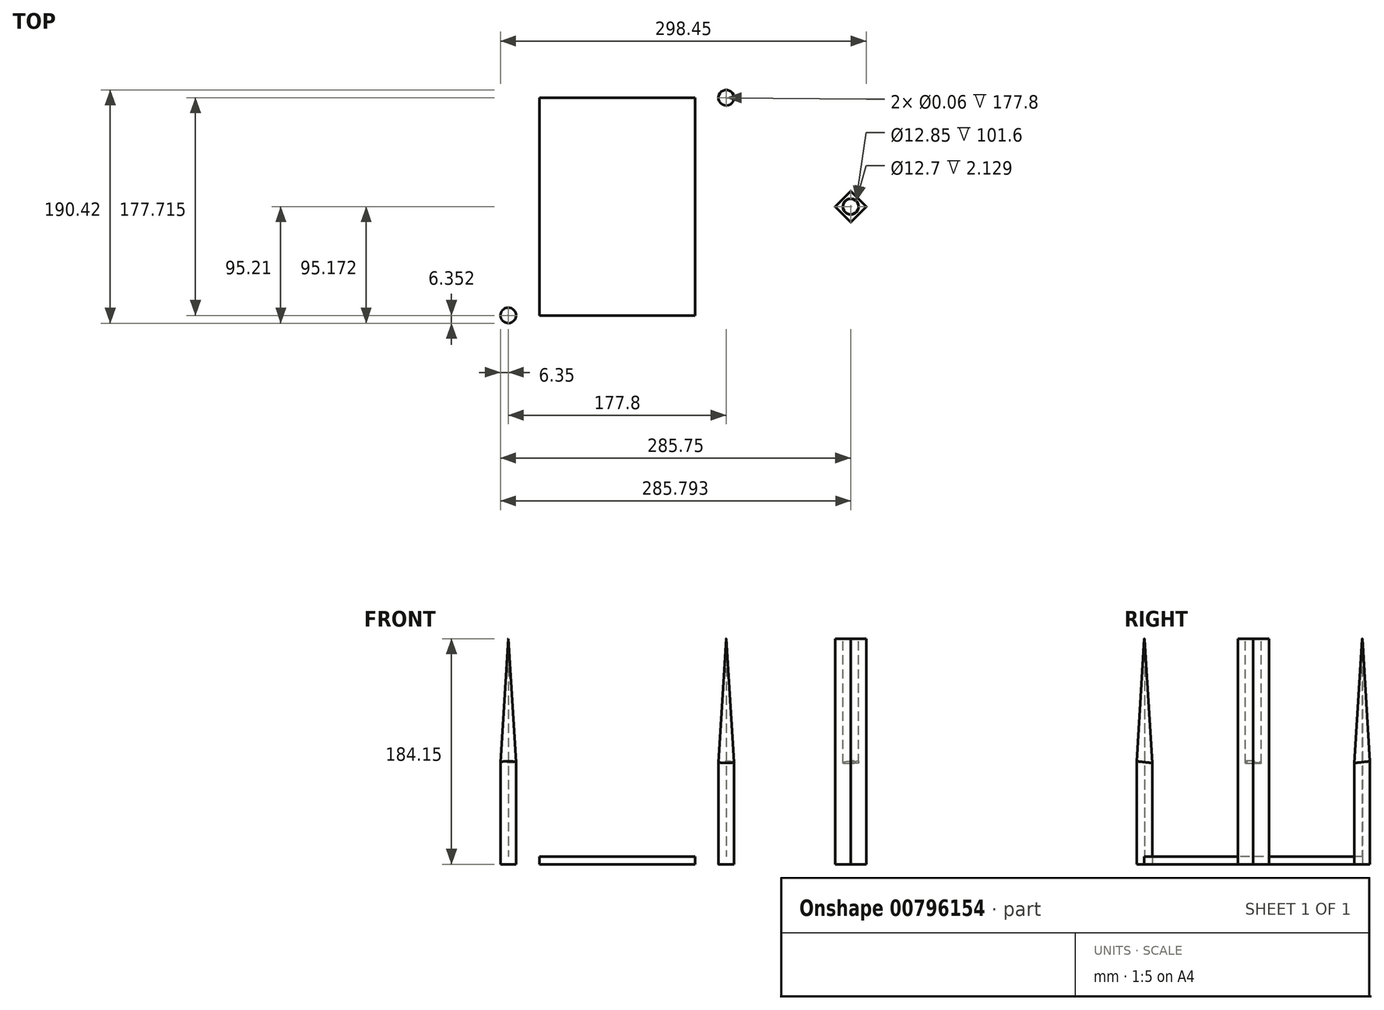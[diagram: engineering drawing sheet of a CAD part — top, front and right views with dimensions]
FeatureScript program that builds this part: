
annotation { "Feature Type Name" : "Feature", "Feature Type Description" : "" }
export const myFeature = defineFeature(function(context is Context, id is Id, definition is map)
    precondition{}
    {
        {
            var Q0;
            Q0=qCreatedBy(makeId("Top.planeOp"),FACE);
            var sketch = newSketch(context, id + "F0", { "sketchPlane" : qUnion([Q0])});
            skLineSegment(sketch, "E0", {"start": v(0, 88.9) * mm, "end": v(-63.5, 88.9) * mm});
            skLineSegment(sketch, "E1", {"start": v(-63.5, 88.9) * mm, "end": v(-88.9, 114.3) * mm});
            skLineSegment(sketch, "E2", {"start": v(-88.9, 114.3) * mm, "end": v(-114.3, 88.9) * mm});
            skLineSegment(sketch, "E3", {"start": v(-114.3, 88.9) * mm, "end": v(-88.9, 63.5) * mm});
            skLineSegment(sketch, "E4", {"start": v(-88.9, 63.5) * mm, "end": v(-63.5, 88.9) * mm});
            skLineSegment(sketch, "E5", {"start": v(-88.9, 63.5) * mm, "end": v(-88.9, 0) * mm});
            skLineSegment(sketch, "E6", {"start": v(-88.9, 88.9) * mm, "end": v(-190.5, 0) * mm});
            skLineSegment(sketch, "E7", {"start": v(-88.9, 114.3) * mm, "end": v(-88.9, 63.5) * mm, "construction": true});
            skLineSegment(sketch, "E8", {"start": v(-63.5, 88.9) * mm, "end": v(-114.3, 88.9) * mm, "construction": true});
            skLineSegment(sketch, "E9", {"start": v(-190.5, 25.4) * mm, "end": v(-215.9, 0) * mm});
            skLineSegment(sketch, "E10", {"start": v(-190.5, 25.4) * mm, "end": v(-165.1, 0) * mm});
            skLineSegment(sketch, "E11", {"start": v(-190.5, 25.4) * mm, "end": v(-190.5, 0) * mm, "construction": true});
            skPoint(sketch, "E12", {"position": v(-190.5, 0) * mm});
            skLineSegment(sketch, "E13.MirrorCS", {"start": v(-114.3, -88.9) * mm, "end": v(-88.9, -63.5) * mm});
            skLineSegment(sketch, "E14.MirrorCS", {"start": v(-88.9, -63.5) * mm, "end": v(-63.5, -88.9) * mm});
            skLineSegment(sketch, "E15.MirrorCS", {"start": v(-63.5, -88.9) * mm, "end": v(-114.3, -88.9) * mm, "construction": true});
            skLineSegment(sketch, "E16.MirrorCS", {"start": v(-190.5, -25.4) * mm, "end": v(-165.1, 0) * mm});
            skLineSegment(sketch, "E17.MirrorCS", {"start": v(-63.5, -88.9) * mm, "end": v(-88.9, -114.3) * mm});
            skLineSegment(sketch, "E18.MirrorCS", {"start": v(-88.9, -114.3) * mm, "end": v(-88.9, -63.5) * mm, "construction": true});
            skLineSegment(sketch, "E19.MirrorCS", {"start": v(0, -88.9) * mm, "end": v(-63.5, -88.9) * mm});
            skLineSegment(sketch, "E20.MirrorCS", {"start": v(-88.9, -114.3) * mm, "end": v(-114.3, -88.9) * mm});
            skLineSegment(sketch, "E21.MirrorCS", {"start": v(-190.5, -25.4) * mm, "end": v(-215.9, 0) * mm});
            skLineSegment(sketch, "E22.MirrorCS", {"start": v(-88.9, -88.9) * mm, "end": v(-190.5, 0) * mm});
            skLineSegment(sketch, "E23.MirrorCS", {"start": v(-190.5, -25.4) * mm, "end": v(-190.5, 0) * mm, "construction": true});
            skLineSegment(sketch, "E24.MirrorCS", {"start": v(-88.9, -63.5) * mm, "end": v(-88.9, 0) * mm});
            skPoint(sketch, "E25.MirrorP", {"position": v(190.5, 0) * mm});
            skLineSegment(sketch, "E26.MirrorCS", {"start": v(63.5, 88.9) * mm, "end": v(114.3, 88.9) * mm, "construction": true});
            skLineSegment(sketch, "E27.MirrorCS", {"start": v(190.5, 25.4) * mm, "end": v(215.9, 0) * mm});
            skLineSegment(sketch, "E28.MirrorCS", {"start": v(63.5, -88.9) * mm, "end": v(114.3, -88.9) * mm, "construction": true});
            skLineSegment(sketch, "E29.MirrorCS", {"start": v(88.9, -63.5) * mm, "end": v(63.5, -88.9) * mm});
            skLineSegment(sketch, "E30.MirrorCS", {"start": v(190.5, 25.4) * mm, "end": v(165.1, 0) * mm});
            skLineSegment(sketch, "E31.MirrorCS", {"start": v(190.5, 25.4) * mm, "end": v(190.5, 0) * mm, "construction": true});
            skLineSegment(sketch, "E32.MirrorCS", {"start": v(114.3, -88.9) * mm, "end": v(88.9, -63.5) * mm});
            skLineSegment(sketch, "E33.MirrorCS", {"start": v(88.9, -63.5) * mm, "end": v(88.9, 0) * mm});
            skLineSegment(sketch, "E34.MirrorCS", {"start": v(190.5, -25.4) * mm, "end": v(190.5, 0) * mm, "construction": true});
            skLineSegment(sketch, "E35.MirrorCS", {"start": v(190.5, -25.4) * mm, "end": v(215.9, 0) * mm});
            skLineSegment(sketch, "E36.MirrorCS", {"start": v(190.5, -25.4) * mm, "end": v(165.1, 0) * mm});
            skLineSegment(sketch, "E37.MirrorCS", {"start": v(0, 88.9) * mm, "end": v(63.5, 88.9) * mm});
            skLineSegment(sketch, "E38.MirrorCS", {"start": v(114.3, 88.9) * mm, "end": v(88.9, 63.5) * mm});
            skLineSegment(sketch, "E39.MirrorCS", {"start": v(88.9, 63.5) * mm, "end": v(63.5, 88.9) * mm});
            skLineSegment(sketch, "E40.MirrorCS", {"start": v(88.9, -88.9) * mm, "end": v(190.5, 0) * mm});
            skLineSegment(sketch, "E41.MirrorCS", {"start": v(88.9, 114.3) * mm, "end": v(88.9, 63.5) * mm, "construction": true});
            skLineSegment(sketch, "E42.MirrorCS", {"start": v(0, -88.9) * mm, "end": v(63.5, -88.9) * mm});
            skLineSegment(sketch, "E43.MirrorCS", {"start": v(63.5, 88.9) * mm, "end": v(88.9, 114.3) * mm});
            skLineSegment(sketch, "E44.MirrorCS", {"start": v(88.9, 114.3) * mm, "end": v(114.3, 88.9) * mm});
            skLineSegment(sketch, "E45.MirrorCS", {"start": v(63.5, -88.9) * mm, "end": v(88.9, -114.3) * mm});
            skLineSegment(sketch, "E46.MirrorCS", {"start": v(88.9, 88.9) * mm, "end": v(190.5, 0) * mm});
            skLineSegment(sketch, "E47.MirrorCS", {"start": v(88.9, -114.3) * mm, "end": v(114.3, -88.9) * mm});
            skLineSegment(sketch, "E48.MirrorCS", {"start": v(88.9, 63.5) * mm, "end": v(88.9, 0) * mm});
            skLineSegment(sketch, "E49.MirrorCS", {"start": v(88.9, -114.3) * mm, "end": v(88.9, -63.5) * mm, "construction": true});
            skSolve(sketch);
        }
        {
            var Q0;
            {var subQ5=sQuery(id+"F0.wireOp",EDGE,"E9");Q0=makeQuery(id+"F0.imprint","IMPRINT",FACE,{"disambiguationData":[TD([[makeQuery(id+"F0.imprint","IMPRINT",EDGE,{"derivedFrom":subQ5}),1.0]])]});}
            var Q1;
            {var subQ0=sQuery(id+"F0.wireOp",EDGE,"E22.MirrorCS");var subQ1=sQuery(id+"F0.wireOp",EDGE,"E6");var subQ2=makeQuery(id+"F0.imprint","INTERSECT",VERTEX,{"derivedFrom":[subQ1,subQ0]});Q1=makeQuery(id+"F0.imprint","IMPRINT",FACE,{"disambiguationData":[TD([[makeQuery(id+"F0.imprint","IMPRINT",EDGE,{"disambiguationData":[TD([[subQ2,1.0]])],"derivedFrom":subQ1}),1.0]])]});}
            var Q2;
            {var subQ7=sQuery(id+"F0.wireOp",EDGE,"E5");Q2=makeQuery(id+"F0.imprint","IMPRINT",FACE,{"disambiguationData":[TD([[makeQuery(id+"F0.imprint","IMPRINT",EDGE,{"derivedFrom":subQ7}),-1.0]])]});}
            var Q3;
            Q3=makeQuery(id+"F0.imprint","IMPRINT",FACE,{"disambiguationData":[TD([[makeQuery(id+"F0.imprint","IMPRINT",EDGE,{"derivedFrom":sQuery(id+"F0.wireOp",EDGE,"E1")}),1.0]])]});
            var Q4;
            {var subQ0=sQuery(id+"F0.wireOp",EDGE,"E14.MirrorCS");Q4=makeQuery(id+"F0.imprint","IMPRINT",FACE,{"disambiguationData":[TD([[makeQuery(id+"F0.imprint","IMPRINT",EDGE,{"derivedFrom":subQ0}),-1.0]])]});}
            var Q5;
            {var subQ1=sQuery(id+"F0.wireOp",EDGE,"E29.MirrorCS");Q5=makeQuery(id+"F0.imprint","IMPRINT",FACE,{"disambiguationData":[TD([[makeQuery(id+"F0.imprint","IMPRINT",EDGE,{"derivedFrom":subQ1}),1.0]])]});}
            var Q6;
            {var subQ9=sQuery(id+"F0.wireOp",EDGE,"E33.MirrorCS");Q6=makeQuery(id+"F0.imprint","IMPRINT",FACE,{"disambiguationData":[TD([[makeQuery(id+"F0.imprint","IMPRINT",EDGE,{"derivedFrom":subQ9}),-1.0]])]});}
            var Q7;
            Q7=makeQuery(id+"F0.imprint","IMPRINT",FACE,{"disambiguationData":[TD([[makeQuery(id+"F0.imprint","IMPRINT",EDGE,{"derivedFrom":sQuery(id+"F0.wireOp",EDGE,"E0")}),1.0]])]});
            var Q8;
            {var subQ0=sQuery(id+"F0.wireOp",EDGE,"E39.MirrorCS");Q8=makeQuery(id+"F0.imprint","IMPRINT",FACE,{"disambiguationData":[TD([[makeQuery(id+"F0.imprint","IMPRINT",EDGE,{"derivedFrom":subQ0}),-1.0]])]});}
            var Q9;
            {var subQ5=sQuery(id+"F0.wireOp",EDGE,"E27.MirrorCS");Q9=makeQuery(id+"F0.imprint","IMPRINT",FACE,{"disambiguationData":[TD([[makeQuery(id+"F0.imprint","IMPRINT",EDGE,{"derivedFrom":subQ5}),-1.0]])]});}
            var Q10;
            {var subQ0=sQuery(id+"F0.wireOp",EDGE,"E36.MirrorCS");var subQ1=sQuery(id+"F0.wireOp",EDGE,"E30.MirrorCS");var subQ2=makeQuery(id+"F0.imprint","INTERSECT",VERTEX,{"derivedFrom":[subQ1,subQ0]});Q10=makeQuery(id+"F0.imprint","IMPRINT",FACE,{"disambiguationData":[TD([[makeQuery(id+"F0.imprint","IMPRINT",EDGE,{"disambiguationData":[TD([[subQ2,1.0]])],"derivedFrom":subQ1}),1.0]])]});}
            extrude(context, id + "F1", {"entities" : qUnion([Q0, Q1, Q2, Q3, Q4, Q5, Q6, Q7, Q8, Q9, Q10]), "depth" : 228.6 * mm, "offsetDistance" : 25.4 * mm});
        }
        {
            var Q0;
            Q0=makeQuery(id+"F1.opExtrude","CAP_FACE",FACE,{"disambiguationData":[OSD([sQuery(id+"F0.wireOp",EDGE,"E0"),sQuery(id+"F0.wireOp",EDGE,"E1"),sQuery(id+"F0.wireOp",EDGE,"E2"),sQuery(id+"F0.wireOp",EDGE,"E3"),sQuery(id+"F0.wireOp",EDGE,"E6"),sQuery(id+"F0.wireOp",EDGE,"E9"),sQuery(id+"F0.wireOp",EDGE,"E10"),sQuery(id+"F0.wireOp",EDGE,"E13.MirrorCS"),sQuery(id+"F0.wireOp",EDGE,"E16.MirrorCS"),sQuery(id+"F0.wireOp",EDGE,"E17.MirrorCS"),sQuery(id+"F0.wireOp",EDGE,"E19.MirrorCS"),sQuery(id+"F0.wireOp",EDGE,"E20.MirrorCS"),sQuery(id+"F0.wireOp",EDGE,"E21.MirrorCS"),sQuery(id+"F0.wireOp",EDGE,"E22.MirrorCS"),sQuery(id+"F0.wireOp",EDGE,"E27.MirrorCS"),sQuery(id+"F0.wireOp",EDGE,"E30.MirrorCS"),sQuery(id+"F0.wireOp",EDGE,"E32.MirrorCS"),sQuery(id+"F0.wireOp",EDGE,"E35.MirrorCS"),sQuery(id+"F0.wireOp",EDGE,"E36.MirrorCS"),sQuery(id+"F0.wireOp",EDGE,"E37.MirrorCS"),sQuery(id+"F0.wireOp",EDGE,"E38.MirrorCS"),sQuery(id+"F0.wireOp",EDGE,"E40.MirrorCS"),sQuery(id+"F0.wireOp",EDGE,"E42.MirrorCS"),sQuery(id+"F0.wireOp",EDGE,"E43.MirrorCS"),sQuery(id+"F0.wireOp",EDGE,"E44.MirrorCS"),sQuery(id+"F0.wireOp",EDGE,"E45.MirrorCS"),sQuery(id+"F0.wireOp",EDGE,"E46.MirrorCS"),sQuery(id+"F0.wireOp",EDGE,"E47.MirrorCS")])],"isStart":false});
            var sketch = newSketch(context, id + "F2", { "sketchPlane" : qUnion([Q0])});
            skLineSegment(sketch, "E50", {"start": v(-101.6, 88.9) * mm, "end": v(-88.9, 76.2) * mm});
            skLineSegment(sketch, "E51", {"start": v(-88.9, 76.2) * mm, "end": v(-76.2, 88.9) * mm});
            skLineSegment(sketch, "E52", {"start": v(-76.2, 88.9) * mm, "end": v(-88.9, 101.6) * mm});
            skLineSegment(sketch, "E53", {"start": v(-88.9, 101.6) * mm, "end": v(-101.6, 88.9) * mm});
            skCircle(sketch, "E54", {"center": v(-88.9, 88.86) * mm, "radius": 6.35 * mm});
            skCircle(sketch, "E55", {"center": v(-88.9, 88.86) * mm, "radius": 0.03 * mm});
            skCircle(sketch, "E56.MirrorC", {"center": v(-88.9, -88.86) * mm, "radius": 0.03 * mm});
            skCircle(sketch, "E57.MirrorC", {"center": v(-88.9, -88.86) * mm, "radius": 6.35 * mm});
            skLineSegment(sketch, "E58.MirrorCS", {"start": v(-88.9, -101.6) * mm, "end": v(-101.6, -88.9) * mm});
            skLineSegment(sketch, "E59.MirrorCS", {"start": v(-76.2, -88.9) * mm, "end": v(-88.9, -101.6) * mm});
            skLineSegment(sketch, "E60.MirrorCS", {"start": v(-88.9, -76.2) * mm, "end": v(-76.2, -88.9) * mm});
            skLineSegment(sketch, "E61.MirrorCS", {"start": v(-101.6, -88.9) * mm, "end": v(-88.9, -76.2) * mm});
            skCircle(sketch, "E62.MirrorC", {"center": v(88.9, 88.86) * mm, "radius": 0.03 * mm});
            skCircle(sketch, "E63.MirrorC", {"center": v(88.9, -88.86) * mm, "radius": 0.03 * mm});
            skCircle(sketch, "E64.MirrorC", {"center": v(88.9, 88.86) * mm, "radius": 6.35 * mm});
            skLineSegment(sketch, "E65.MirrorCS", {"start": v(88.9, 101.6) * mm, "end": v(101.6, 88.9) * mm});
            skLineSegment(sketch, "E66.MirrorCS", {"start": v(76.2, 88.9) * mm, "end": v(88.9, 101.6) * mm});
            skLineSegment(sketch, "E67.MirrorCS", {"start": v(88.9, 76.2) * mm, "end": v(76.2, 88.9) * mm});
            skLineSegment(sketch, "E68.MirrorCS", {"start": v(101.6, 88.9) * mm, "end": v(88.9, 76.2) * mm});
            skLineSegment(sketch, "E69.MirrorCS", {"start": v(101.6, -88.9) * mm, "end": v(88.9, -76.2) * mm});
            skLineSegment(sketch, "E70.MirrorCS", {"start": v(76.2, -88.9) * mm, "end": v(88.9, -101.6) * mm});
            skLineSegment(sketch, "E71.MirrorCS", {"start": v(88.9, -76.2) * mm, "end": v(76.2, -88.9) * mm});
            skCircle(sketch, "E72.MirrorC", {"center": v(88.9, -88.86) * mm, "radius": 6.35 * mm});
            skLineSegment(sketch, "E73.MirrorCS", {"start": v(88.9, -101.6) * mm, "end": v(101.6, -88.9) * mm});
            skLineSegment(sketch, "E74", {"start": v(-190.5, 12.7) * mm, "end": v(-203.2, 0) * mm});
            skLineSegment(sketch, "E75", {"start": v(-203.2, 0) * mm, "end": v(-190.5, -12.7) * mm});
            skLineSegment(sketch, "E76", {"start": v(-190.5, -12.7) * mm, "end": v(-177.8, 0) * mm});
            skLineSegment(sketch, "E77", {"start": v(-190.5, 12.7) * mm, "end": v(-177.8, 0) * mm});
            skCircle(sketch, "E78", {"center": v(-190.5, 0) * mm, "radius": 6.35 * mm});
            skCircle(sketch, "E79.MirrorC", {"center": v(190.5, 0) * mm, "radius": 6.35 * mm});
            skLineSegment(sketch, "E80.MirrorCS", {"start": v(203.2, 0) * mm, "end": v(190.5, -12.7) * mm});
            skLineSegment(sketch, "E81.MirrorCS", {"start": v(190.5, 12.7) * mm, "end": v(177.8, 0) * mm});
            skLineSegment(sketch, "E82.MirrorCS", {"start": v(190.5, -12.7) * mm, "end": v(177.8, 0) * mm});
            skLineSegment(sketch, "E83.MirrorCS", {"start": v(190.5, 12.7) * mm, "end": v(203.2, 0) * mm});
            skSolve(sketch);
        }
        {
            var Q0;
            Q0=makeQuery(id+"F2.imprint","IMPRINT",FACE,{"disambiguationData":[TD([[makeQuery(id+"F2.imprint","IMPRINT",EDGE,{"derivedFrom":sQuery(id+"F2.wireOp",EDGE,"E74")}),1.0]])]});
            var Q1;
            Q1=makeQuery(id+"F2.imprint","IMPRINT",FACE,{"disambiguationData":[TD([[makeQuery(id+"F2.imprint","IMPRINT",EDGE,{"derivedFrom":sQuery(id+"F2.wireOp",EDGE,"E50")}),1.0]])]});
            var Q2;
            Q2=makeQuery(id+"F2.imprint","IMPRINT",FACE,{"disambiguationData":[TD([[makeQuery(id+"F2.imprint","IMPRINT",EDGE,{"derivedFrom":sQuery(id+"F2.wireOp",EDGE,"E79.MirrorC")}),1.0]])]});
            var Q3;
            Q3=makeQuery(id+"F2.imprint","IMPRINT",FACE,{"disambiguationData":[TD([[makeQuery(id+"F2.imprint","IMPRINT",EDGE,{"derivedFrom":sQuery(id+"F2.wireOp",EDGE,"E69.MirrorCS")}),1.0]])]});
            var Q4;
            Q4=makeQuery(id+"F2.imprint","IMPRINT",FACE,{"disambiguationData":[TD([[makeQuery(id+"F2.imprint","IMPRINT",EDGE,{"derivedFrom":sQuery(id+"F2.wireOp",EDGE,"E57.MirrorC")}),1.0]])]});
            var Q5;
            Q5=makeQuery(id+"F2.imprint","IMPRINT",FACE,{"disambiguationData":[TD([[makeQuery(id+"F2.imprint","IMPRINT",EDGE,{"derivedFrom":sQuery(id+"F2.wireOp",EDGE,"E64.MirrorC")}),1.0]])]});
            extrude(context, id + "F3", {"entities" : qUnion([Q0, Q1, Q2, Q3, Q4, Q5]), "operationType" : NewBodyOperationType.ADD, "depth" : 76.2 * mm, "offsetDistance" : 25.4 * mm});
        }
        {
            var Q0;
            Q0=makeQuery(id+"F2.imprint","IMPRINT",FACE,{"disambiguationData":[TD([[makeQuery(id+"F2.imprint","IMPRINT",EDGE,{"derivedFrom":sQuery(id+"F2.wireOp",EDGE,"E54")}),1.0]])]});
            var Q1;
            Q1=makeQuery(id+"F2.imprint","IMPRINT",FACE,{"disambiguationData":[TD([[makeQuery(id+"F2.imprint","IMPRINT",EDGE,{"derivedFrom":sQuery(id+"F2.wireOp",EDGE,"E79.MirrorC")}),-1.0]])]});
            var Q2;
            Q2=makeQuery(id+"F2.imprint","IMPRINT",FACE,{"disambiguationData":[TD([[makeQuery(id+"F2.imprint","IMPRINT",EDGE,{"derivedFrom":sQuery(id+"F2.wireOp",EDGE,"E56.MirrorC")}),-1.0]])]});
            var Q3;
            Q3=makeQuery(id+"F2.imprint","IMPRINT",FACE,{"disambiguationData":[TD([[makeQuery(id+"F2.imprint","IMPRINT",EDGE,{"derivedFrom":sQuery(id+"F2.wireOp",EDGE,"E63.MirrorC")}),1.0]])]});
            var Q4;
            Q4=makeQuery(id+"F2.imprint","IMPRINT",FACE,{"disambiguationData":[TD([[makeQuery(id+"F2.imprint","IMPRINT",EDGE,{"derivedFrom":sQuery(id+"F2.wireOp",EDGE,"E62.MirrorC")}),-1.0]])]});
            extrude(context, id + "F4", {"entities" : qUnion([Q0, Q1, Q2, Q3, Q4]), "operationType" : NewBodyOperationType.ADD, "depth" : 177.8 * mm, "offsetDistance" : 25.4 * mm});
        }
        {
            var Q0;
            Q0=makeQuery(id+"F2.imprint","IMPRINT",FACE,{"disambiguationData":[TD([[makeQuery(id+"F2.imprint","IMPRINT",EDGE,{"derivedFrom":sQuery(id+"F2.wireOp",EDGE,"E78")}),1.0]])]});
            extrude(context, id + "F5", {"entities" : qUnion([Q0]), "operationType" : NewBodyOperationType.ADD, "depth" : 203.2 * mm, "offsetDistance" : 25.4 * mm});
        }
        {
            var Q0;
            Q0=makeQuery(id+"F1.opExtrude","SWEPT_FACE",FACE,{"disambiguationData":[OSD([sQuery(id+"F0.wireOp",EDGE,"E19.MirrorCS"),sQuery(id+"F0.wireOp",EDGE,"E42.MirrorCS")])]});
            var sketch = newSketch(context, id + "F6", { "sketchPlane" : qUnion([Q0])});
            skLineSegment(sketch, "E84.bottom", {"start": v(-88.9, 304.8) * mm, "end": v(-82.5, 304.8) * mm});
            skLineSegment(sketch, "E84.top", {"start": v(-88.9, 406.4) * mm, "end": v(-82.5, 406.4) * mm});
            skLineSegment(sketch, "E84.left", {"start": v(-88.9, 304.8) * mm, "end": v(-88.9, 406.4) * mm});
            skLineSegment(sketch, "E84.right", {"start": v(-82.5, 304.8) * mm, "end": v(-82.5, 406.4) * mm});
            skLineSegment(sketch, "E85", {"start": v(-88.87, 406.4) * mm, "end": v(-82.5, 304.8) * mm});
            skSolve(sketch);
        }
        {
            var Q0;
            {var subQ0=sQuery(id+"F6.wireOp",EDGE,"E84.right");Q0=makeQuery(id+"F6.imprint","IMPRINT",FACE,{"disambiguationData":[TD([[makeQuery(id+"F6.imprint","IMPRINT",EDGE,{"derivedFrom":subQ0}),1.0]])]});}
            var Q1;
            Q1=sQuery(id+"F6.wireOp",EDGE,"E84.left");
            revolve(context, id + "F7", {"operationType" : NewBodyOperationType.REMOVE, "surfaceOperationType" : NewSurfaceOperationType.NEW, "entities" : qUnion([Q0]), "axis" : qUnion([Q1]), "revolveType" : RevolveType.FULL, "oppositeDirection" : true});
        }
        {
            var Q0;
            Q0=makeQuery(id+"F1.opExtrude","SWEPT_FACE",FACE,{"disambiguationData":[OSD([sQuery(id+"F0.wireOp",EDGE,"E19.MirrorCS"),sQuery(id+"F0.wireOp",EDGE,"E42.MirrorCS")])]});
            var sketch = newSketch(context, id + "F8", { "sketchPlane" : qUnion([Q0])});
            skLineSegment(sketch, "E86.bottom", {"start": v(88.9, 304.8) * mm, "end": v(95.3, 304.8) * mm});
            skLineSegment(sketch, "E86.top", {"start": v(88.9, 406.4) * mm, "end": v(95.3, 406.4) * mm});
            skLineSegment(sketch, "E86.left", {"start": v(88.9, 304.8) * mm, "end": v(88.9, 406.4) * mm});
            skLineSegment(sketch, "E86.right", {"start": v(95.3, 304.8) * mm, "end": v(95.3, 406.4) * mm});
            skLineSegment(sketch, "E87", {"start": v(88.93, 406.4) * mm, "end": v(95.3, 304.8) * mm});
            skSolve(sketch);
        }
        {
            var Q0;
            {var subQ0=sQuery(id+"F8.wireOp",EDGE,"E86.right");Q0=makeQuery(id+"F8.imprint","IMPRINT",FACE,{"disambiguationData":[TD([[makeQuery(id+"F8.imprint","IMPRINT",EDGE,{"derivedFrom":subQ0}),1.0]])]});}
            var Q1;
            Q1=sQuery(id+"F8.wireOp",EDGE,"E86.left");
            revolve(context, id + "F9", {"operationType" : NewBodyOperationType.REMOVE, "surfaceOperationType" : NewSurfaceOperationType.NEW, "entities" : qUnion([Q0]), "axis" : qUnion([Q1]), "revolveType" : RevolveType.FULL, "oppositeDirection" : true});
        }
        {
            var Q0;
            Q0=makeQuery(id+"F1.opExtrude","SWEPT_FACE",FACE,{"disambiguationData":[OSD([sQuery(id+"F0.wireOp",EDGE,"E0"),sQuery(id+"F0.wireOp",EDGE,"E37.MirrorCS")])]});
            var sketch = newSketch(context, id + "F10", { "sketchPlane" : qUnion([Q0])});
            skLineSegment(sketch, "E88.bottom", {"start": v(88.9, 304.8) * mm, "end": v(95.3, 304.8) * mm});
            skLineSegment(sketch, "E88.top", {"start": v(88.9, 406.4) * mm, "end": v(95.3, 406.4) * mm});
            skLineSegment(sketch, "E88.left", {"start": v(88.9, 304.8) * mm, "end": v(88.9, 406.4) * mm});
            skLineSegment(sketch, "E88.right", {"start": v(95.3, 304.8) * mm, "end": v(95.3, 406.4) * mm});
            skLineSegment(sketch, "E89", {"start": v(88.93, 406.4) * mm, "end": v(95.3, 304.8) * mm});
            skSolve(sketch);
        }
        {
            var Q0;
            {var subQ0=sQuery(id+"F10.wireOp",EDGE,"E88.right");Q0=makeQuery(id+"F10.imprint","IMPRINT",FACE,{"disambiguationData":[TD([[makeQuery(id+"F10.imprint","IMPRINT",EDGE,{"derivedFrom":subQ0}),1.0]])]});}
            var Q1;
            Q1=sQuery(id+"F10.wireOp",EDGE,"E88.left");
            revolve(context, id + "F11", {"operationType" : NewBodyOperationType.REMOVE, "surfaceOperationType" : NewSurfaceOperationType.NEW, "entities" : qUnion([Q0]), "axis" : qUnion([Q1]), "revolveType" : RevolveType.FULL, "oppositeDirection" : true});
        }
        {
            var Q0;
            Q0=makeQuery(id+"F1.opExtrude","SWEPT_FACE",FACE,{"disambiguationData":[OSD([sQuery(id+"F0.wireOp",EDGE,"E0"),sQuery(id+"F0.wireOp",EDGE,"E37.MirrorCS")])]});
            var sketch = newSketch(context, id + "F12", { "sketchPlane" : qUnion([Q0])});
            skLineSegment(sketch, "E90.bottom", {"start": v(-82.5, 304.8) * mm, "end": v(-88.9, 304.8) * mm});
            skLineSegment(sketch, "E90.top", {"start": v(-82.5, 406.4) * mm, "end": v(-88.9, 406.4) * mm});
            skLineSegment(sketch, "E90.left", {"start": v(-82.5, 304.8) * mm, "end": v(-82.5, 406.4) * mm});
            skLineSegment(sketch, "E90.right", {"start": v(-88.9, 304.8) * mm, "end": v(-88.9, 406.4) * mm});
            skLineSegment(sketch, "E91", {"start": v(-88.87, 406.4) * mm, "end": v(-82.5, 304.8) * mm});
            skSolve(sketch);
        }
        {
            var Q0;
            {var subQ0=sQuery(id+"F12.wireOp",EDGE,"E90.left");Q0=makeQuery(id+"F12.imprint","IMPRINT",FACE,{"disambiguationData":[TD([[makeQuery(id+"F12.imprint","IMPRINT",EDGE,{"derivedFrom":subQ0}),1.0]])]});}
            var Q1;
            Q1=sQuery(id+"F12.wireOp",EDGE,"E90.right");
            revolve(context, id + "F13", {"operationType" : NewBodyOperationType.REMOVE, "surfaceOperationType" : NewSurfaceOperationType.NEW, "entities" : qUnion([Q0]), "axis" : qUnion([Q1]), "revolveType" : RevolveType.FULL, "oppositeDirection" : true});
        }
        {
            var Q0;
            Q0=makeQuery(id+"F1.opExtrude","SWEPT_FACE",FACE,{"disambiguationData":[OSD([sQuery(id+"F0.wireOp",EDGE,"E46.MirrorCS")])]});
            var sketch = newSketch(context, id + "F14", { "sketchPlane" : qUnion([Q0])});
            skLineSegment(sketch, "E92.bottom", {"start": v(-143.42, 304.8) * mm, "end": v(-137, 304.8) * mm});
            skLineSegment(sketch, "E92.top", {"start": v(-143.42, 406.4) * mm, "end": v(-137, 406.4) * mm});
            skLineSegment(sketch, "E92.left", {"start": v(-143.42, 304.8) * mm, "end": v(-143.42, 406.4) * mm});
            skLineSegment(sketch, "E92.right", {"start": v(-137, 304.8) * mm, "end": v(-137, 406.4) * mm});
            skLineSegment(sketch, "E93", {"start": v(-143.4, 406.4) * mm, "end": v(-137, 304.8) * mm});
            skSolve(sketch);
        }
        {
            var Q0;
            {var subQ0=sQuery(id+"F14.wireOp",EDGE,"E92.right");Q0=makeQuery(id+"F14.imprint","IMPRINT",FACE,{"disambiguationData":[TD([[makeQuery(id+"F14.imprint","IMPRINT",EDGE,{"derivedFrom":subQ0}),1.0]])]});}
            var Q1;
            Q1=sQuery(id+"F14.wireOp",EDGE,"E92.left");
            revolve(context, id + "F15", {"operationType" : NewBodyOperationType.REMOVE, "surfaceOperationType" : NewSurfaceOperationType.NEW, "entities" : qUnion([Q0]), "axis" : qUnion([Q1]), "revolveType" : RevolveType.FULL, "oppositeDirection" : true});
        }
        {
            var Q0;
            Q0=makeQuery(id+"F1.opExtrude","SWEPT_FACE",FACE,{"disambiguationData":[OSD([sQuery(id+"F0.wireOp",EDGE,"E22.MirrorCS")])]});
            var sketch = newSketch(context, id + "F16", { "sketchPlane" : qUnion([Q0])});
            skLineSegment(sketch, "E94.bottom", {"start": v(-143.42, 304.8) * mm, "end": v(-137, 304.8) * mm});
            skLineSegment(sketch, "E94.top", {"start": v(-143.42, 431.8) * mm, "end": v(-137, 431.8) * mm});
            skLineSegment(sketch, "E94.left", {"start": v(-143.42, 304.8) * mm, "end": v(-143.42, 431.8) * mm});
            skLineSegment(sketch, "E94.right", {"start": v(-137, 304.8) * mm, "end": v(-137, 431.8) * mm});
            skLineSegment(sketch, "E95", {"start": v(-143.4, 431.8) * mm, "end": v(-137, 304.8) * mm});
            skSolve(sketch);
        }
        {
            var Q0;
            {var subQ0=sQuery(id+"F16.wireOp",EDGE,"E94.right");Q0=makeQuery(id+"F16.imprint","IMPRINT",FACE,{"disambiguationData":[TD([[makeQuery(id+"F16.imprint","IMPRINT",EDGE,{"derivedFrom":subQ0}),1.0]])]});}
            var Q1;
            Q1=sQuery(id+"F16.wireOp",EDGE,"E94.left");
            revolve(context, id + "F17", {"operationType" : NewBodyOperationType.REMOVE, "surfaceOperationType" : NewSurfaceOperationType.NEW, "entities" : qUnion([Q0]), "axis" : qUnion([Q1]), "revolveType" : RevolveType.FULL, "oppositeDirection" : true});
        }
        {
            var Q0;
            Q0=qCreatedBy(makeId("Front.planeOp"),FACE);
            var sketch = newSketch(context, id + "F18", { "sketchPlane" : qUnion([Q0])});
            skLineSegment(sketch, "E96.bottom", {"start": v(-228.6, 222.25) * mm, "end": v(228.6, 222.25) * mm});
            skLineSegment(sketch, "E96.top", {"start": v(-228.6, -12.7) * mm, "end": v(228.6, -12.7) * mm});
            skLineSegment(sketch, "E96.left", {"start": v(-228.6, 222.25) * mm, "end": v(-228.6, -12.7) * mm});
            skLineSegment(sketch, "E96.right", {"start": v(228.6, 222.25) * mm, "end": v(228.6, -12.7) * mm});
            skSolve(sketch);
        }
        {
            var Q0;
            Q0=qSketchRegion(id+"F18",true);
            extrude(context, id + "F19", {"entities" : qUnion([Q0]), "operationType" : NewBodyOperationType.REMOVE, "endBound" : BoundingType.SYMMETRIC, "oppositeDirection" : true, "depth" : 508 * mm, "offsetDistance" : 25.4 * mm});
        }
        {
            var Q0;
            {var subQ0=sQuery(id+"F0.wireOp",EDGE,"E43.MirrorCS");var subQ1=sQuery(id+"F0.wireOp",EDGE,"E40.MirrorCS");var subQ2=sQuery(id+"F0.wireOp",EDGE,"E38.MirrorCS");var subQ3=sQuery(id+"F0.wireOp",EDGE,"E32.MirrorCS");var subQ4=sQuery(id+"F0.wireOp",EDGE,"E47.MirrorCS");var subQ5=sQuery(id+"F0.wireOp",EDGE,"E46.MirrorCS");var subQ6=sQuery(id+"F0.wireOp",EDGE,"E45.MirrorCS");var subQ7=sQuery(id+"F0.wireOp",EDGE,"E44.MirrorCS");var subQ8=sQuery(id+"F0.wireOp",EDGE,"E17.MirrorCS");var subQ9=sQuery(id+"F0.wireOp",EDGE,"E16.MirrorCS");var subQ10=sQuery(id+"F0.wireOp",EDGE,"E13.MirrorCS");var subQ11=sQuery(id+"F0.wireOp",EDGE,"E10");var subQ12=sQuery(id+"F0.wireOp",EDGE,"E9");var subQ13=sQuery(id+"F0.wireOp",EDGE,"E6");var subQ14=sQuery(id+"F0.wireOp",EDGE,"E37.MirrorCS");var subQ15=sQuery(id+"F0.wireOp",EDGE,"E0");var subQ16=sQuery(id+"F0.wireOp",EDGE,"E1");var subQ17=sQuery(id+"F0.wireOp",EDGE,"E2");var subQ18=sQuery(id+"F0.wireOp",EDGE,"E3");var subQ19=sQuery(id+"F0.wireOp",EDGE,"E42.MirrorCS");var subQ20=sQuery(id+"F0.wireOp",EDGE,"E19.MirrorCS");var subQ21=sQuery(id+"F0.wireOp",EDGE,"E20.MirrorCS");var subQ22=sQuery(id+"F0.wireOp",EDGE,"E21.MirrorCS");var subQ23=sQuery(id+"F0.wireOp",EDGE,"E22.MirrorCS");var subQ24=sQuery(id+"F0.wireOp",EDGE,"E27.MirrorCS");var subQ25=sQuery(id+"F0.wireOp",EDGE,"E30.MirrorCS");var subQ26=sQuery(id+"F0.wireOp",EDGE,"E35.MirrorCS");var subQ27=sQuery(id+"F0.wireOp",EDGE,"E36.MirrorCS");Q0=makeQuery(id+"F3.boolean.opBoolean","SPLIT",FACE,{"disambiguationData":[TD([makeQuery(id+"F1.opExtrude","SWEPT_FACE",FACE,{"disambiguationData":[OSD([subQ16])]})])],"derivedFrom":makeQuery(id+"F1.opExtrude","CAP_FACE",FACE,{"disambiguationData":[OSD([subQ15,subQ16,subQ17,subQ18,subQ13,subQ12,subQ11,subQ10,subQ9,subQ8,subQ20,subQ21,subQ22,subQ23,subQ24,subQ25,subQ3,subQ26,subQ27,subQ14,subQ2,subQ1,subQ19,subQ0,subQ7,subQ6,subQ5,subQ4])],"isStart":false})});}
            var sketch = newSketch(context, id + "F20", { "sketchPlane" : qUnion([Q0])});
            skLineSegment(sketch, "E97.bottom", {"start": v(63.5, 138.04) * mm, "end": v(246.98, 138.04) * mm});
            skLineSegment(sketch, "E97.top", {"start": v(63.5, -133.06) * mm, "end": v(246.98, -133.06) * mm});
            skLineSegment(sketch, "E97.left", {"start": v(63.5, 138.04) * mm, "end": v(63.5, -133.06) * mm});
            skLineSegment(sketch, "E97.right", {"start": v(246.98, 138.04) * mm, "end": v(246.98, -133.06) * mm});
            skLineSegment(sketch, "E98.bottom", {"start": v(-63.5, 130.16) * mm, "end": v(-229.15, 130.16) * mm});
            skLineSegment(sketch, "E98.top", {"start": v(-63.5, -150.07) * mm, "end": v(-229.15, -150.07) * mm});
            skLineSegment(sketch, "E98.left", {"start": v(-63.5, 130.16) * mm, "end": v(-63.5, -150.07) * mm});
            skLineSegment(sketch, "E98.right", {"start": v(-229.15, 130.16) * mm, "end": v(-229.15, -150.07) * mm});
            skSolve(sketch);
        }
        {
            var Q0;
            {var subQ0=makeQuery(id+"F1.opExtrude","CAP_EDGE",EDGE,{"disambiguationData":[OSD([sQuery(id+"F0.wireOp",EDGE,"E1")])],"isStart":false});Q0=makeQuery(id+"F20.imprint","IMPRINT",FACE,{"disambiguationData":[TD([[makeQuery(id+"F20.imprint","IMPRINT",EDGE,{"derivedFrom":subQ0}),1.0]])]});}
            var Q1;
            Q1=makeQuery(id+"F20.imprint","IMPRINT",FACE,{"disambiguationData":[TD([[makeQuery(id+"F20.imprint","IMPRINT",EDGE,{"derivedFrom":makeQuery(id+"F3.opExtrude","CAP_EDGE",EDGE,{"disambiguationData":[OSD([sQuery(id+"F2.wireOp",EDGE,"E50")])],"isStart":true})}),1.0]])]});
            var Q2;
            Q2=makeQuery(id+"F20.imprint","IMPRINT",FACE,{"disambiguationData":[TD([[makeQuery(id+"F20.imprint","IMPRINT",EDGE,{"derivedFrom":makeQuery(id+"F3.opExtrude","CAP_EDGE",EDGE,{"disambiguationData":[OSD([sQuery(id+"F2.wireOp",EDGE,"E74")])],"isStart":true})}),1.0]])]});
            var Q3;
            Q3=makeQuery(id+"F20.imprint","IMPRINT",FACE,{"disambiguationData":[TD([[makeQuery(id+"F20.imprint","IMPRINT",EDGE,{"derivedFrom":makeQuery(id+"F3.opExtrude","CAP_EDGE",EDGE,{"disambiguationData":[OSD([sQuery(id+"F2.wireOp",EDGE,"E58.MirrorCS")])],"isStart":true})}),-1.0]])]});
            var Q4;
            {var subQ1=sQuery(id+"F20.wireOp",EDGE,"E98.bottom");Q4=makeQuery(id+"F20.imprint","IMPRINT",FACE,{"disambiguationData":[TD([[makeQuery(id+"F20.imprint","IMPRINT",EDGE,{"derivedFrom":subQ1}),1.0]])]});}
            extrude(context, id + "F21", {"entities" : qUnion([Q0, Q1, Q2, Q3, Q4]), "operationType" : NewBodyOperationType.REMOVE, "endBound" : BoundingType.SYMMETRIC, "oppositeDirection" : true, "depth" : 508 * mm, "offsetDistance" : 25.4 * mm});
        }
        {
            var Q0;
            Q0=makeQuery(id+"F20.imprint","IMPRINT",FACE,{"disambiguationData":[TD([[makeQuery(id+"F20.imprint","IMPRINT",EDGE,{"derivedFrom":makeQuery(id+"F1.opExtrude","CAP_EDGE",EDGE,{"disambiguationData":[OSD([sQuery(id+"F0.wireOp",EDGE,"E27.MirrorCS")])],"isStart":false})}),-1.0]])]});
            var Q1;
            Q1=makeQuery(id+"F20.imprint","IMPRINT",FACE,{"disambiguationData":[TD([[makeQuery(id+"F20.imprint","IMPRINT",EDGE,{"derivedFrom":makeQuery(id+"F3.opExtrude","CAP_EDGE",EDGE,{"disambiguationData":[OSD([sQuery(id+"F2.wireOp",EDGE,"E65.MirrorCS")])],"isStart":true})}),-1.0]])]});
            var Q2;
            {var subQ3=sQuery(id+"F20.wireOp",EDGE,"E97.bottom");Q2=makeQuery(id+"F20.imprint","IMPRINT",FACE,{"disambiguationData":[TD([[makeQuery(id+"F20.imprint","IMPRINT",EDGE,{"derivedFrom":subQ3}),-1.0]])]});}
            var Q3;
            Q3=makeQuery(id+"F20.imprint","IMPRINT",FACE,{"disambiguationData":[TD([[makeQuery(id+"F20.imprint","IMPRINT",EDGE,{"derivedFrom":makeQuery(id+"F3.opExtrude","CAP_EDGE",EDGE,{"disambiguationData":[OSD([sQuery(id+"F2.wireOp",EDGE,"E80.MirrorCS")])],"isStart":true})}),-1.0]])]});
            var Q4;
            Q4=makeQuery(id+"F20.imprint","IMPRINT",FACE,{"disambiguationData":[TD([[makeQuery(id+"F20.imprint","IMPRINT",EDGE,{"derivedFrom":makeQuery(id+"F3.opExtrude","CAP_EDGE",EDGE,{"disambiguationData":[OSD([sQuery(id+"F2.wireOp",EDGE,"E69.MirrorCS")])],"isStart":true})}),1.0]])]});
            extrude(context, id + "F22", {"entities" : qUnion([Q0, Q1, Q2, Q3, Q4]), "operationType" : NewBodyOperationType.REMOVE, "endBound" : BoundingType.SYMMETRIC, "oppositeDirection" : true, "depth" : 508 * mm, "offsetDistance" : 25.4 * mm});
        }
    });
